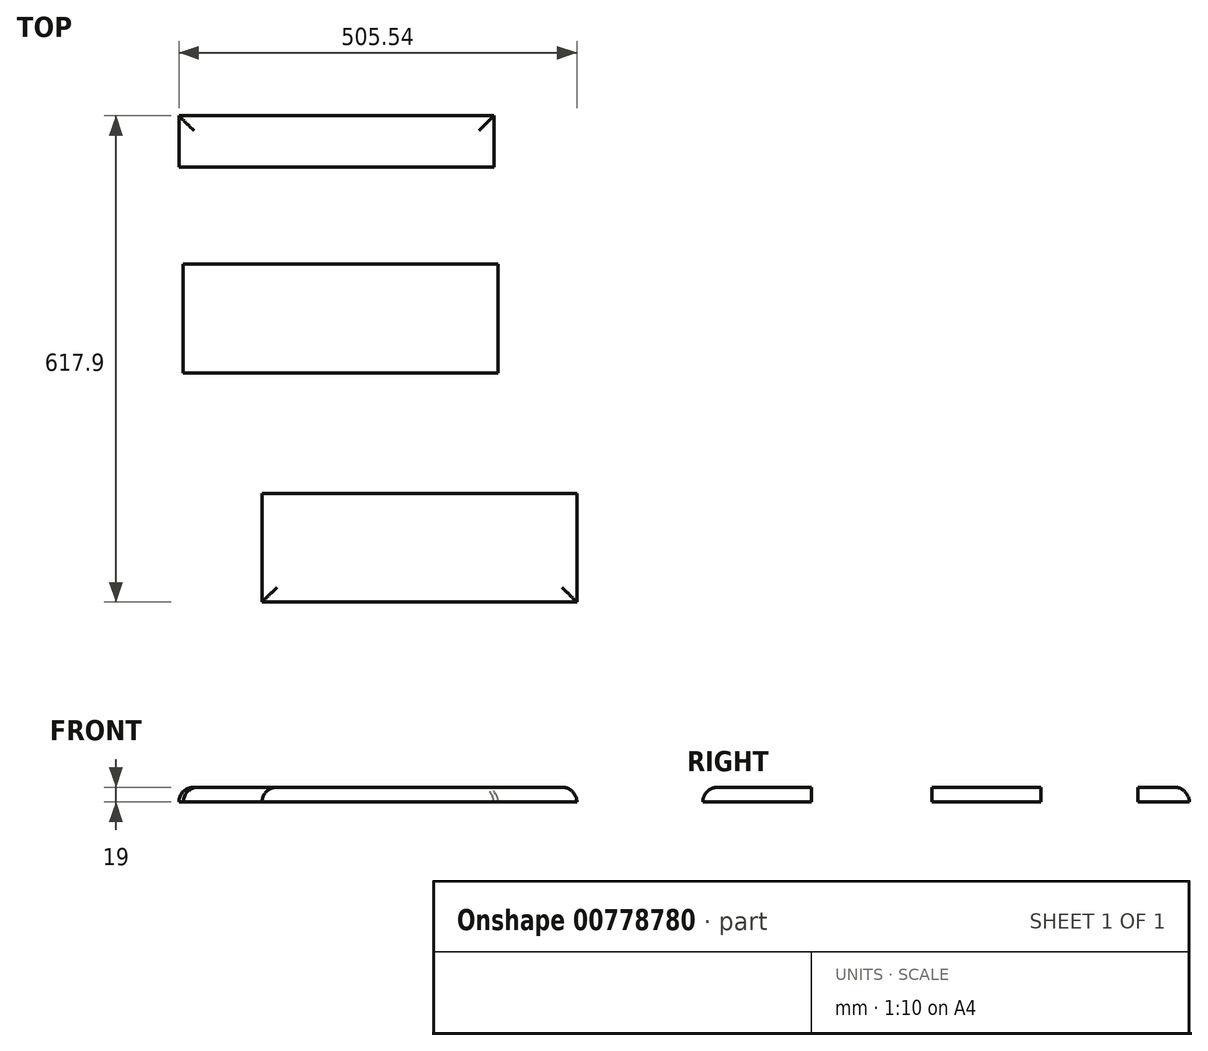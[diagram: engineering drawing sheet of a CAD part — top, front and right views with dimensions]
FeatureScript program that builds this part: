
annotation { "Feature Type Name" : "Feature", "Feature Type Description" : "" }
export const myFeature = defineFeature(function(context is Context, id is Id, definition is map)
    precondition{}
    {
        {
            var Q0;
            Q0=qCreatedBy(makeId("Top.planeOp"),FACE);
            var sketch = newSketch(context, id + "F0", { "sketchPlane" : qUnion([Q0])});
            skLineSegment(sketch, "E0.bottom", {"start": v(-160.31, 62.9) * mm, "end": v(239.69, 62.9) * mm});
            skLineSegment(sketch, "E0.top", {"start": v(-160.31, -75.1) * mm, "end": v(239.69, -75.1) * mm});
            skLineSegment(sketch, "E0.left", {"start": v(-160.31, 62.9) * mm, "end": v(-160.31, -75.1) * mm});
            skLineSegment(sketch, "E0.right", {"start": v(239.69, 62.9) * mm, "end": v(239.69, -75.1) * mm});
            skSolve(sketch);
        }
        {
            var Q0;
            Q0=qCreatedBy(makeId("Top.planeOp"),FACE);
            var sketch = newSketch(context, id + "F1", { "sketchPlane" : qUnion([Q0])});
            skLineSegment(sketch, "E1.bottom", {"start": v(-60.31, -228.34) * mm, "end": v(339.69, -228.34) * mm});
            skLineSegment(sketch, "E1.top", {"start": v(-60.31, -366.34) * mm, "end": v(339.69, -366.34) * mm});
            skLineSegment(sketch, "E1.left", {"start": v(-60.31, -228.34) * mm, "end": v(-60.31, -366.34) * mm});
            skLineSegment(sketch, "E1.right", {"start": v(339.69, -228.34) * mm, "end": v(339.69, -366.34) * mm});
            skSolve(sketch);
        }
        {
            var Q0;
            Q0=qCreatedBy(makeId("Top.planeOp"),FACE);
            var sketch = newSketch(context, id + "F2", { "sketchPlane" : qUnion([Q0])});
            skLineSegment(sketch, "E2.bottom", {"start": v(-165.85, 251.56) * mm, "end": v(234.15, 251.56) * mm});
            skLineSegment(sketch, "E2.top", {"start": v(-165.85, 186.56) * mm, "end": v(234.15, 186.56) * mm});
            skLineSegment(sketch, "E2.left", {"start": v(-165.85, 251.56) * mm, "end": v(-165.85, 186.56) * mm});
            skLineSegment(sketch, "E2.right", {"start": v(234.15, 251.56) * mm, "end": v(234.15, 186.56) * mm});
            skSolve(sketch);
        }
        {
            var Q0;
            Q0=makeQuery(id+"F2.imprint","IMPRINT",FACE,{"disambiguationData":[TD([[makeQuery(id+"F2.imprint","IMPRINT",EDGE,{"derivedFrom":sQuery(id+"F2.wireOp",EDGE,"E2.bottom")}),-1.0]])]});
            extrude(context, id + "F3", {"entities" : qUnion([Q0]), "depth" : 19 * mm, "offsetDistance" : 25 * mm});
        }
        {
            var Q0;
            Q0=makeQuery(id+"F0.imprint","IMPRINT",FACE,{"disambiguationData":[TD([[makeQuery(id+"F0.imprint","IMPRINT",EDGE,{"derivedFrom":sQuery(id+"F0.wireOp",EDGE,"E0.bottom")}),-1.0]])]});
            extrude(context, id + "F4", {"entities" : qUnion([Q0]), "depth" : 19 * mm, "offsetDistance" : 25 * mm});
        }
        {
            var Q0;
            Q0=makeQuery(id+"F1.imprint","IMPRINT",FACE,{"disambiguationData":[TD([[makeQuery(id+"F1.imprint","IMPRINT",EDGE,{"derivedFrom":sQuery(id+"F1.wireOp",EDGE,"E1.bottom")}),-1.0]])]});
            extrude(context, id + "F5", {"entities" : qUnion([Q0]), "depth" : 19 * mm, "offsetDistance" : 25 * mm});
        }
        {
            var Q0;
            Q0=makeQuery(id+"F5.opExtrude","CAP_EDGE",EDGE,{"disambiguationData":[OSD([sQuery(id+"F1.wireOp",EDGE,"E1.top")])],"isStart":false});
            var Q1;
            Q1=makeQuery(id+"F5.opExtrude","CAP_EDGE",EDGE,{"disambiguationData":[OSD([sQuery(id+"F1.wireOp",EDGE,"E1.left")])],"isStart":false});
            var Q2;
            Q2=makeQuery(id+"F5.opExtrude","CAP_EDGE",EDGE,{"disambiguationData":[OSD([sQuery(id+"F1.wireOp",EDGE,"E1.right")])],"isStart":false});
            var Q3;
            Q3=makeQuery(id+"F4.opExtrude","CAP_EDGE",EDGE,{"disambiguationData":[OSD([sQuery(id+"F0.wireOp",EDGE,"E0.left")])],"isStart":false});
            var Q4;
            Q4=makeQuery(id+"F4.opExtrude","CAP_EDGE",EDGE,{"disambiguationData":[OSD([sQuery(id+"F0.wireOp",EDGE,"E0.right")])],"isStart":false});
            var Q5;
            Q5=makeQuery(id+"F3.opExtrude","CAP_EDGE",EDGE,{"disambiguationData":[OSD([sQuery(id+"F2.wireOp",EDGE,"E2.right")])],"isStart":false});
            var Q6;
            Q6=makeQuery(id+"F3.opExtrude","CAP_EDGE",EDGE,{"disambiguationData":[OSD([sQuery(id+"F2.wireOp",EDGE,"E2.bottom")])],"isStart":false});
            var Q7;
            Q7=makeQuery(id+"F3.opExtrude","CAP_EDGE",EDGE,{"disambiguationData":[OSD([sQuery(id+"F2.wireOp",EDGE,"E2.left")])],"isStart":false});
            fillet(context, id + "F6", {"entities" : qUnion([Q0, Q1, Q2, Q3, Q4, Q5, Q6, Q7]), "radius" : 19 * mm, "tangentPropagation" : true, "allowEdgeOverflow" : false});
        }
    });
